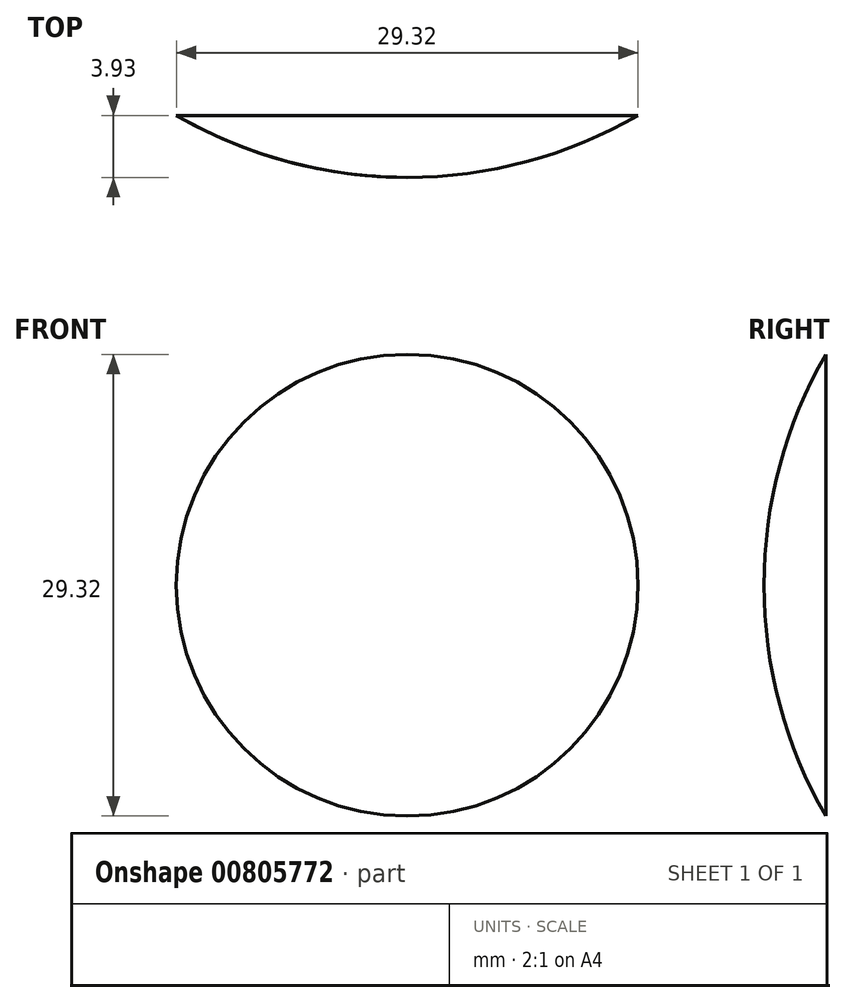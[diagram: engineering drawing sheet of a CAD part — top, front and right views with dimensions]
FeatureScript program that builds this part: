
annotation { "Feature Type Name" : "Feature", "Feature Type Description" : "" }
export const myFeature = defineFeature(function(context is Context, id is Id, definition is map)
    precondition{}
    {
        {
            var Q0;
            Q0=qCreatedBy(makeId("Top.planeOp"),FACE);
            var sketch = newSketch(context, id + "F0", { "sketchPlane" : qUnion([Q0])});
            skLineSegment(sketch, "E0", {"start": v(0, 0) * mm, "end": v(0, 12.7) * mm});
            skLineSegment(sketch, "E1.MirrorCS", {"start": v(0, 0) * mm, "end": v(0, -12.7) * mm});
            skLineSegment(sketch, "E2", {"start": v(0, 12.7) * mm, "end": v(14.66, -12.7) * mm});
            skLineSegment(sketch, "E3.MirrorCS", {"start": v(0, 12.7) * mm, "end": v(-14.66, -12.7) * mm});
            skLineSegment(sketch, "E4", {"start": v(-14.66, -12.7) * mm, "end": v(14.66, -12.7) * mm});
            skArc(sketch, "E5", {"start": v(0, 12.7) * mm, "mid": v(10.74, 1.96) * mm, "end": v(14.66, -12.7) * mm});
            skArc(sketch, "E6.MirrorCS", {"start": v(0, 12.7) * mm, "mid": v(-10.74, 1.96) * mm, "end": v(-14.66, -12.7) * mm});
            skArc(sketch, "E7", {"start": v(-14.66, -12.7) * mm, "mid": v(0, -16.63) * mm, "end": v(14.66, -12.7) * mm});
            skLineSegment(sketch, "E8", {"start": v(0, -12.7) * mm, "end": v(0, -16.63) * mm});
            skSolve(sketch);
        }
        {
            var Q0;
            Q0=sQuery(id+"F0.wireOp",EDGE,"E6.MirrorCS");
            var Q1;
            Q1=sQuery(id+"F0.wireOp",EDGE,"E1.MirrorCS");
            revolve(context, id + "F1", {"bodyType" : ToolBodyType.SURFACE, "surfaceOperationType" : NewSurfaceOperationType.NEW, "surfaceEntities" : qUnion([Q0]), "axis" : qUnion([Q1]), "revolveType" : RevolveType.FULL});
        }
        {
            var Q0;
            {var subQ0=sQuery(id+"F0.wireOp",EDGE,"E8");Q0=makeQuery(id+"F0.imprint","IMPRINT",FACE,{"disambiguationData":[TD([[makeQuery(id+"F0.imprint","IMPRINT",EDGE,{"derivedFrom":subQ0}),-1.0]])]});}
            var Q1;
            Q1=sQuery(id+"F0.wireOp",EDGE,"E8");
            revolve(context, id + "F2", {"surfaceOperationType" : NewSurfaceOperationType.NEW, "entities" : qUnion([Q0]), "axis" : qUnion([Q1]), "revolveType" : RevolveType.FULL});
        }
    });
